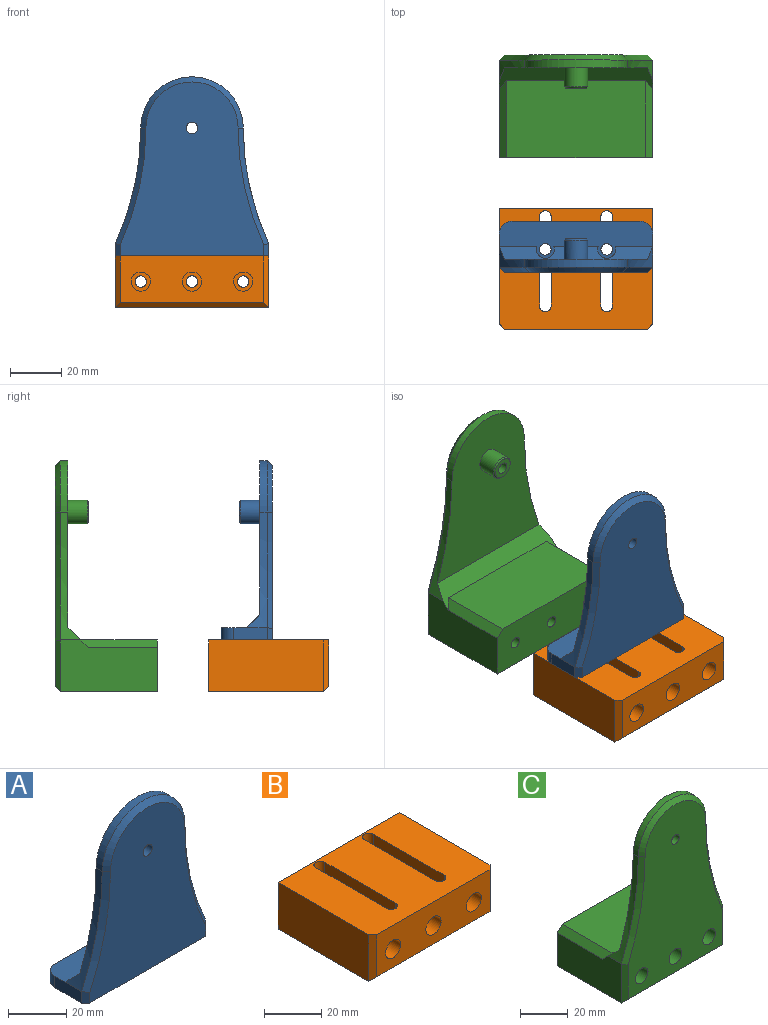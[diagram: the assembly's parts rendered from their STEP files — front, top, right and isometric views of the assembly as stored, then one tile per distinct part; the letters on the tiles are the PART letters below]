
ASSEMBLY  parts=3 mates=2
PART A: 26 faces, bbox 60x20x70 mm
  f0: cylinder r=2.25mm len=4.78mm, axis (0,0,-1), area 67.6mm2, adj f3,f4
  f1: cylinder r=2.25mm len=4.78mm, axis (0,0,-1), area 67.6mm2, adj f3,f4
  f2: plane 60x5mm, normal (0,0.71,0.71), area 334.6mm2, adj f4,f6,f8,f11,f24,f25
  f3: plane 60x20mm, normal (0,0,-1), area 1153.5mm2, adj f0,f1,f5,f9,f12,f13,f14,f15
  f4: plane 60x14.5mm, normal (0,0,1), area 609.8mm2, adj f0,f1,f2,f5,f9,f13,f14,f15
  f5: plane 13x4.78mm, normal (1,0,0), area 62.1mm2, adj f3,f4,f6,f14,f16
  f6: cylinder r=107.25mm len=45.22mm, axis (0,-1,0), area 153.7mm2, adj f2,f5,f7,f11,f17
  f7: cylinder r=20mm len=40mm, axis (0,-1,0), area 188.5mm2, adj f6,f8,f11,f19
  f8: cylinder r=107.25mm len=45.22mm, axis (0,-1,0), area 153.7mm2, adj f2,f7,f9,f11,f20
  f9: plane 13x4.78mm, normal (-1,0,0), area 62.1mm2, adj f3,f4,f8,f15,f18
  f10: cylinder r=2.25mm len=13mm, axis (0,-1,0), area 183.8mm2, adj f12,f22
  f11: plane 60.22x55.66mm, normal (0,1,0), area 2377.4mm2, adj f2,f6,f7,f8,f21
  f12: plane 68x56mm, normal (0,-1,0), area 2678.4mm2, adj f3,f10,f16,f17,f18,f19,f20
  f13: plane 50x4.78mm, normal (0,1,0), area 238.9mm2, adj f3,f4,f14,f15
  f14: cylinder r=5mm len=5mm, axis (0,0,-1), area 37.5mm2, adj f3,f4,f5,f13
  f15: cylinder r=5mm len=5mm, axis (0,0,1), area 37.5mm2, adj f3,f4,f9,f13
  f16: plane 4.78x2mm, normal (0.71,-0.71,0), area 12.9mm2, adj f3,f5,f12,f17
  f17: cone r=109.25mm half-angle=45deg, axis (0,-1,0), area 132.6mm2, adj f6,f12,f16,f19
  f18: plane 4.78x2mm, normal (-0.71,-0.71,0), area 12.9mm2, adj f3,f9,f12,f20
  f19: cone r=20mm half-angle=45deg, axis (0,1,0), area 168.8mm2, adj f7,f12,f17,f20
  f20: cone r=107.25mm half-angle=45deg, axis (0,-1,0), area 132.6mm2, adj f8,f12,f18,f19
  f21: cylinder r=4.6mm len=9.2mm, axis (0,-1,0), area 216.8mm2, adj f11,f23
  f22: plane 8.2x8.2mm, normal (0,1,0), area 36.9mm2, adj f10,f23
  f23: cone r=4.1mm half-angle=45deg, axis (0,-1,0), area 19.3mm2, adj f21,f22
  f24: cylinder r=3.5mm len=7mm, axis (0,0,-1), area 36.5mm2, adj f2,f4
  f25: cylinder r=3.5mm len=7mm, axis (0,0,-1), area 36.5mm2, adj f2,f4
PART B: 34 faces, bbox 60x47x20 mm
  f0: plane 60x47mm, normal (0,0,1), area 2469.2mm2, adj f2,f3,f4,f5,f6,f7,f8,f12
  f1: plane 60x45mm, normal (0,0,-1), area 2082.8mm2, adj f12,f13,f16,f17,f24,f25,f26,f28
  f2: cylinder r=2.25mm len=17.5mm, axis (0,0,-1), area 123.7mm2, adj f0,f3,f4,f31
  f3: plane 35x17.5mm, normal (1,0,0), area 612.5mm2, adj f0,f2,f31,f32
  f4: plane 35x17.5mm, normal (-1,0,0), area 612.5mm2, adj f0,f2,f31,f32
  f5: cylinder r=2.25mm len=17.5mm, axis (0,0,-1), area 123.7mm2, adj f0,f6,f7,f27
  f6: plane 35x17.5mm, normal (-1,0,0), area 612.5mm2, adj f0,f5,f27,f33
  f7: plane 35x17.5mm, normal (1,0,0), area 612.5mm2, adj f0,f5,f27,f33
  f8: plane 56x18mm, normal (0,-1,0), area 875.5mm2, adj f0,f14,f15,f17,f19,f21,f23
  f9: cylinder r=2.25mm len=5mm, axis (0,-1,0), area 70.7mm2, adj f12,f22
  f10: cylinder r=2.25mm len=5mm, axis (0,-1,0), area 70.7mm2, adj f12,f20
  f11: cylinder r=2.25mm len=5mm, axis (0,-1,0), area 70.7mm2, adj f12,f18
  f12: plane 60x20mm, normal (0,1,0), area 1115.3mm2, adj f0,f1,f9,f10,f11,f13,f16,f24
  f13: plane 45x20mm, normal (1,0,0), area 900mm2, adj f0,f1,f12,f14
  f14: plane 20x2mm, normal (0.71,-0.71,0), area 53.7mm2, adj f0,f8,f13,f17
  f15: plane 20x2mm, normal (-0.71,-0.71,0), area 53.7mm2, adj f0,f8,f16,f17
  f16: plane 45x20mm, normal (-1,0,0), area 900mm2, adj f0,f1,f12,f15
  f17: plane 60x2mm, normal (0,-0.71,-0.71), area 164mm2, adj f1,f8,f14,f15
  f18: plane 7.5x7.5mm, normal (0,-1,0), area 28.3mm2, adj f11,f19
  f19: cylinder r=3.75mm len=42mm, axis (0,-1,0), area 989.6mm2, adj f8,f18
  f20: plane 7.5x7.5mm, normal (0,-1,0), area 28.3mm2, adj f10,f21
  f21: cylinder r=3.75mm len=42mm, axis (0,-1,0), area 989.6mm2, adj f8,f20
  f22: plane 7.5x7.5mm, normal (0,-1,0), area 28.3mm2, adj f9,f23
  f23: cylinder r=3.75mm len=42mm, axis (0,-1,0), area 989.6mm2, adj f8,f22
  f24: plane 41.7x2.5mm, normal (-1,0,0), area 104.2mm2, adj f1,f12,f25,f27
  f25: plane 7.4x2.5mm, normal (0,1,0), area 18.5mm2, adj f1,f24,f26,f27
  f26: plane 41.7x2.5mm, normal (1,0,0), area 104.2mm2, adj f1,f12,f25,f27
  f27: plane 41.7x7.4mm, normal (0,0,-1), area 135.2mm2, adj f5,f6,f7,f12,f24,f25,f26,f33
  f28: plane 41.7x2.5mm, normal (-1,0,0), area 104.2mm2, adj f1,f12,f29,f31
  f29: plane 7.4x2.5mm, normal (0,1,0), area 18.5mm2, adj f1,f28,f30,f31
  f30: plane 41.7x2.5mm, normal (1,0,0), area 104.2mm2, adj f1,f12,f29,f31
  f31: plane 41.7x7.4mm, normal (0,0,-1), area 135.2mm2, adj f2,f3,f4,f12,f28,f29,f30,f32
  f32: cylinder r=2.25mm len=17.5mm, axis (0,0,1), area 123.7mm2, adj f0,f3,f4,f31
  f33: cylinder r=2.25mm len=17.5mm, axis (0,0,1), area 123.7mm2, adj f0,f6,f7,f27
PART C: 65 faces, bbox 60x40x90 mm
  f0: cylinder r=2.25mm len=4.6mm, axis (0,1,0), area 65mm2, adj f12,f52,f54,f63,f64
  f1: plane 4.5x1.5mm, normal (0,-1,0), area 5.7mm2, adj f36,f43,f44,f51
  f2: cylinder r=2.25mm len=4.6mm, axis (0,1,0), area 65mm2, adj f12,f48,f58,f59,f61
  f3: plane 4.5x1.5mm, normal (0,-1,0), area 5.7mm2, adj f32,f39,f40,f57
  f4: plane 4.5x1.5mm, normal (0,-1,0), area 5.7mm2, adj f34,f41,f42,f55
  f5: plane 4.5x1.5mm, normal (0,-1,0), area 5.7mm2, adj f36,f43,f44,f53
  f6: plane 6x1.5mm, normal (0,-1,0), area 6.3mm2, adj f32,f39
  f7: plane 6x1.5mm, normal (0,-1,0), area 6.3mm2, adj f34,f42
  f8: plane 6x1.5mm, normal (0,-1,0), area 6.3mm2, adj f36,f44
  f9: plane 6x1.5mm, normal (0,-1,0), area 6.3mm2, adj f32,f40
  f10: cylinder r=2.25mm len=4.6mm, axis (0,1,0), area 65mm2, adj f12,f50,f56,f60,f62
  f11: plane 86x56mm, normal (0,-1,0), area 3491.3mm2, adj f19,f25,f26,f27,f28,f29,f30,f32
  f12: plane 60x20mm, normal (0,1,0), area 1143.3mm2, adj f0,f2,f10,f15,f16,f17,f21,f37
  f13: plane 65x56.07mm, normal (0,1,0), area 2599.9mm2, adj f14,f18,f20,f22,f31
  f14: cylinder r=130mm len=50mm, axis (0,1,0), area 167.4mm2, adj f13,f15,f20,f30,f31
  f15: plane 38x20mm, normal (-1,0,0), area 674.5mm2, adj f12,f14,f16,f28,f31,f38
  f16: plane 60x38mm, normal (0,0,-1), area 2280mm2, adj f12,f15,f17,f26
  f17: plane 38x20mm, normal (1,0,0), area 674.5mm2, adj f12,f16,f18,f25,f31,f37
  f18: cylinder r=130mm len=50mm, axis (0,1,0), area 167.4mm2, adj f13,f17,f20,f27,f31
  f19: cylinder r=2.25mm len=13mm, axis (0,1,0), area 183.8mm2, adj f11,f23
  f20: cylinder r=20mm len=40mm, axis (0,1,0), area 188.5mm2, adj f13,f14,f18,f29
  f21: plane 54x30mm, normal (0,0,1), area 1620mm2, adj f12,f31,f37,f38
  f22: cylinder r=4.6mm len=9.2mm, axis (0,-1,0), area 216.8mm2, adj f13,f24
  f23: plane 8.2x8.2mm, normal (0,1,0), area 36.9mm2, adj f19,f24
  f24: cone r=4.6mm half-angle=45deg, axis (0,-1,0), area 19.3mm2, adj f22,f23
  f25: plane 20x2mm, normal (0.71,-0.71,0), area 53.2mm2, adj f11,f17,f26,f27
  f26: plane 60x2mm, normal (0,-0.71,-0.71), area 164mm2, adj f11,f16,f25,f28
  f27: cone r=132mm half-angle=45deg, axis (0,-1,0), area 145.7mm2, adj f11,f18,f25,f29
  f28: plane 20x2mm, normal (-0.71,-0.71,0), area 53.2mm2, adj f11,f15,f26,f30
  f29: cone r=20mm half-angle=45deg, axis (0,1,0), area 168.8mm2, adj f11,f20,f27,f30
  f30: cone r=130mm half-angle=45deg, axis (0,-1,0), area 145.7mm2, adj f11,f14,f28,f29
  f31: plane 60x8mm, normal (0,0.71,0.71), area 422.8mm2, adj f13,f14,f15,f17,f18,f21,f37,f38
  f32: cylinder r=3.75mm len=35.2mm, axis (0,-1,0), area 826.6mm2, adj f3,f6,f9,f11,f39,f40,f46
  f33: plane 6x1.5mm, normal (0,-1,0), area 6.3mm2, adj f34,f41
  f34: cylinder r=3.75mm len=35.2mm, axis (0,-1,0), area 826.6mm2, adj f4,f7,f11,f33,f41,f42,f45
  f35: plane 6x1.5mm, normal (0,-1,0), area 6.3mm2, adj f36,f43
  f36: cylinder r=3.75mm len=35.2mm, axis (0,-1,0), area 826.6mm2, adj f1,f5,f8,f11,f35,f43,f44
  f37: plane 30x3mm, normal (0.71,0,0.71), area 120.9mm2, adj f12,f17,f21,f31
  f38: plane 30x3mm, normal (-0.71,0,0.71), area 120.9mm2, adj f12,f15,f21,f31
  f39: plane 6x0.4mm, normal (-1,0,0), area 2.1mm2, adj f3,f6,f32,f46,f47,f57,f58,f59
  f40: plane 6x0.4mm, normal (1,0,0), area 2.1mm2, adj f3,f9,f32,f46,f47,f48,f57,f61
  f41: plane 6x0.4mm, normal (-1,0,0), area 2.1mm2, adj f4,f33,f34,f45,f49,f50,f55,f60
  f42: plane 6x0.4mm, normal (1,0,0), area 2.1mm2, adj f4,f7,f34,f45,f49,f55,f56,f62
  f43: plane 6x0.4mm, normal (-1,0,0), area 2.1mm2, adj f1,f5,f35,f36,f51,f52,f53,f64
  f44: plane 6x0.4mm, normal (1,0,0), area 2.1mm2, adj f1,f5,f8,f36,f51,f53,f54,f63
  f45: plane 4.5x1.5mm, normal (0,-1,0), area 5.7mm2, adj f34,f41,f42,f49
  f46: plane 4.5x1.5mm, normal (0,-1,0), area 5.7mm2, adj f32,f39,f40,f47
  f47: plane 4.5x0.2mm, normal (0,0,-1), area 0.9mm2, adj f39,f40,f46,f48,f59
  f48: plane 2.25x2.25mm, normal (0,-1,0), area 1.1mm2, adj f2,f40,f47
  f49: plane 4.5x0.2mm, normal (0,0,1), area 0.9mm2, adj f41,f42,f45,f50,f62
  f50: plane 2.25x2.25mm, normal (0,-1,0), area 1.1mm2, adj f10,f41,f49
  f51: plane 4.5x0.2mm, normal (0,0,-1), area 0.9mm2, adj f1,f43,f44,f52,f63
  f52: plane 2.25x2.25mm, normal (0,-1,0), area 1.1mm2, adj f0,f43,f51
  f53: plane 4.5x0.2mm, normal (0,0,1), area 0.9mm2, adj f5,f43,f44,f54,f64
  f54: plane 2.25x2.25mm, normal (0,-1,0), area 1.1mm2, adj f0,f44,f53
  f55: plane 4.5x0.2mm, normal (0,0,-1), area 0.9mm2, adj f4,f41,f42,f56,f60
  f56: plane 2.25x2.25mm, normal (0,-1,0), area 1.1mm2, adj f10,f42,f55
  f57: plane 4.5x0.2mm, normal (0,0,1), area 0.9mm2, adj f3,f39,f40,f58,f61
  f58: plane 2.25x2.25mm, normal (0,-1,0), area 1.1mm2, adj f2,f39,f57
  f59: plane 2.25x2.25mm, normal (0,-1,0), area 1.1mm2, adj f2,f39,f47
  f60: plane 2.25x2.25mm, normal (0,-1,0), area 1.1mm2, adj f10,f41,f55
  f61: plane 2.25x2.25mm, normal (0,-1,0), area 1.1mm2, adj f2,f40,f57
  f62: plane 2.25x2.25mm, normal (0,-1,0), area 1.1mm2, adj f10,f42,f49
  f63: plane 2.25x2.25mm, normal (0,-1,0), area 1.1mm2, adj f0,f44,f51
  f64: plane 2.25x2.25mm, normal (0,-1,0), area 1.1mm2, adj f0,f43,f53
PLACE A t=(-29.54,-20.53,4.55)mm
PLACE B t=(-29.54,-42.65,4.55)mm fixed
PLACE C rot(axis=(0,0,1),180deg) t=(-29.54,59.35,4.55)mm
MATE planar B.f32 <-> A.f0  axis (0,0,1) through (-17.54,-33.65,24.55)mm
MATE fastened C.f10 <-> B.f10  axis (0,-1,0) through (-29.54,24.35,14.55)mm
